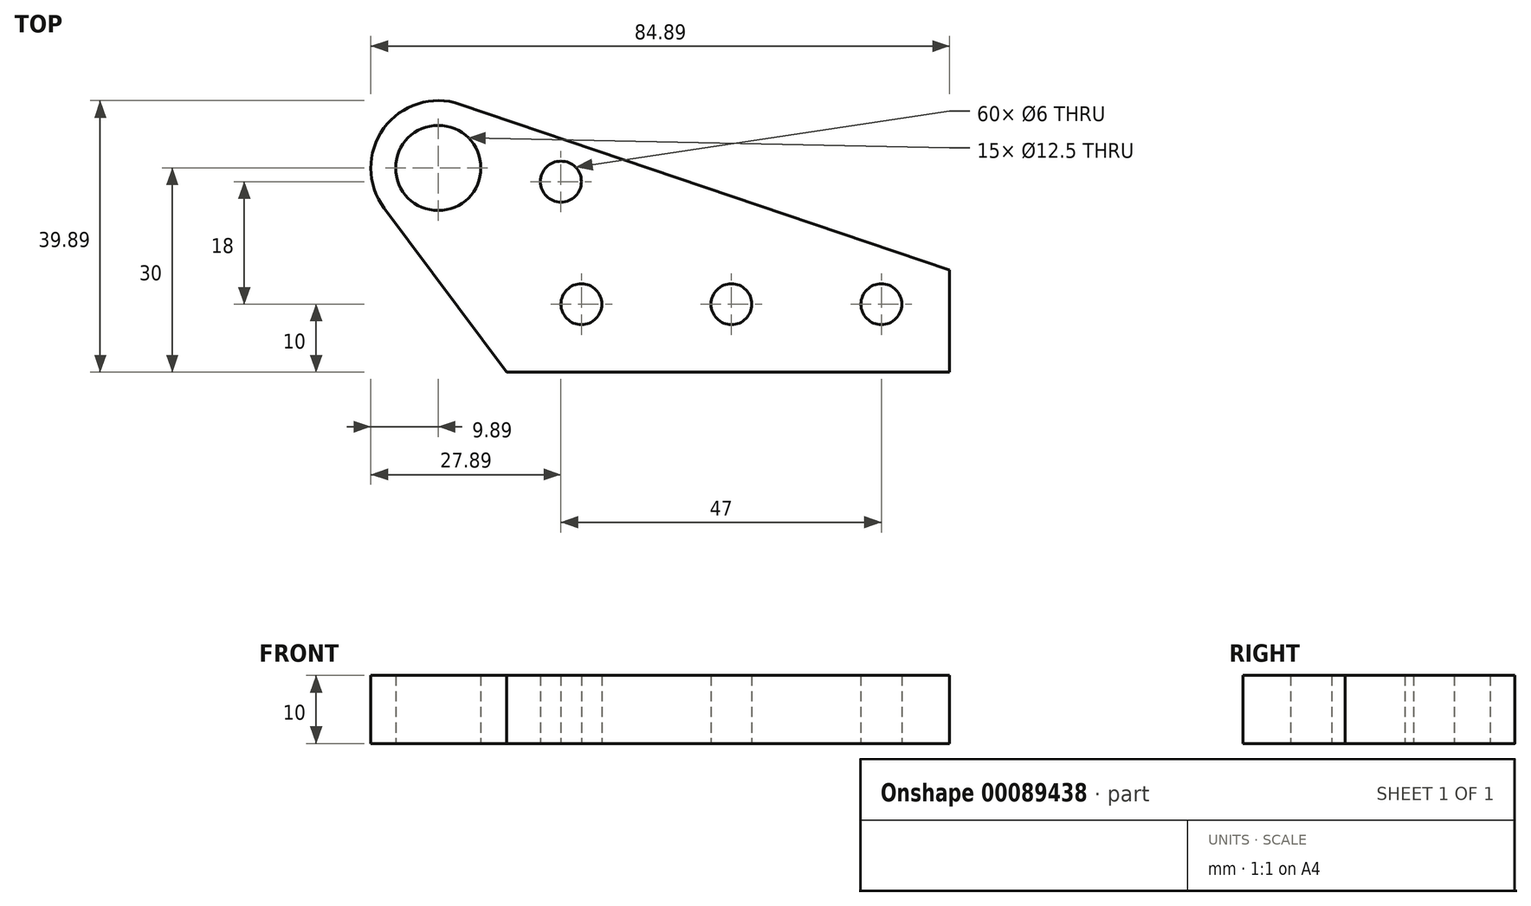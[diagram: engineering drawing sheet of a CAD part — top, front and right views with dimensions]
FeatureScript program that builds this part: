
annotation { "Feature Type Name" : "Feature", "Feature Type Description" : "" }
export const myFeature = defineFeature(function(context is Context, id is Id, definition is map)
    precondition{}
    {
        {
            var Q0;
            Q0=qCreatedBy(makeId("Top.planeOp"),FACE);
            var sketch = newSketch(context, id + "F0", { "sketchPlane" : qUnion([Q0])});
            skLineSegment(sketch, "E0.bottom", {"start": v(0, 0) * mm, "end": v(-65, 0) * mm});
            skLineSegment(sketch, "E0.left", {"start": v(0, 0) * mm, "end": v(0, 15) * mm});
            skCircle(sketch, "E1", {"center": v(-75, 30) * mm, "radius": 6.25 * mm});
            skArc(sketch, "E2", {"start": v(-71.82, 39.36) * mm, "mid": v(-83, 35.82) * mm, "end": v(-82.93, 24.1) * mm});
            skLineSegment(sketch, "E3", {"start": v(-65, 0) * mm, "end": v(-82.93, 24.1) * mm});
            skLineSegment(sketch, "E4", {"start": v(0, 15) * mm, "end": v(-71.82, 39.36) * mm});
            skCircle(sketch, "E5", {"center": v(-10, 10) * mm, "radius": 3 * mm});
            skCircle(sketch, "E6.1.0.0", {"center": v(-32, 10) * mm, "radius": 3 * mm});
            skCircle(sketch, "E6.2.0.0", {"center": v(-54, 10) * mm, "radius": 3 * mm});
            skLineSegment(sketch, "E6.direction1", {"start": v(-10, 10) * mm, "end": v(-32, 10) * mm, "construction": true});
            skCircle(sketch, "E7", {"center": v(-57, 28) * mm, "radius": 3 * mm});
            skSolve(sketch);
        }
        {
            var Q0;
            Q0=makeQuery(id+"F0.imprint","IMPRINT",FACE,{"disambiguationData":[TD([[makeQuery(id+"F0.imprint","IMPRINT",EDGE,{"derivedFrom":sQuery(id+"F0.wireOp",EDGE,"E0.bottom")}),-1.0]])]});
            extrude(context, id + "F1", {"entities" : qUnion([Q0]), "depth" : 10 * mm});
        }
    });
